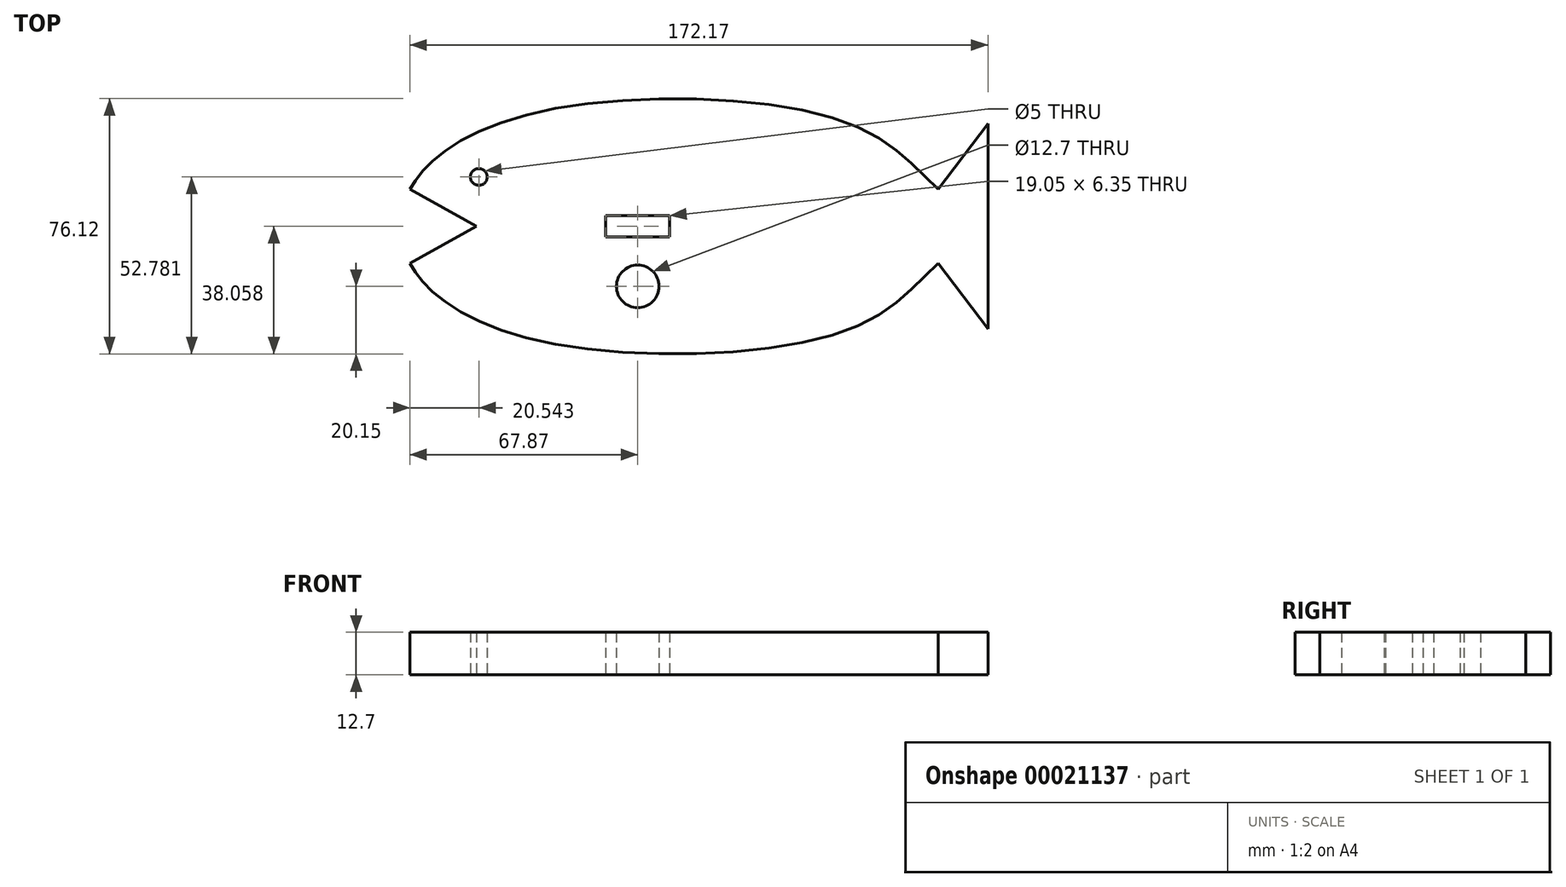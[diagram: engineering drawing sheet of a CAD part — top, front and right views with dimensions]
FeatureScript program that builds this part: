
annotation { "Feature Type Name" : "Feature", "Feature Type Description" : "" }
export const myFeature = defineFeature(function(context is Context, id is Id, definition is map)
    precondition{}
    {
        {
            var Q0;
            Q0=qCreatedBy(makeId("Top.planeOp"),FACE);
            var sketch = newSketch(context, id + "F0", { "sketchPlane" : qUnion([Q0])});
            skFitSpline(sketch, "E0", {"points": [v(89.47, 28.98) * mm, v(63.18, 48.55) * mm, v(-25.37, 52.9) * mm, v(-60.56, 37.87) * mm, v(-67.87, 28.98) * mm], "startDerivative": vector(-90.55, 84.73) * mm, "endDerivative": vector(-33.24, -55.1) * mm});
            skLineSegment(sketch, "E1", {"start": v(-67.87, 28.98) * mm, "end": v(-48.1, 17.9) * mm});
            skLineSegment(sketch, "E2", {"start": v(-48.1, 17.9) * mm, "end": v(104.3, 17.9) * mm, "construction": true});
            skLineSegment(sketch, "E3", {"start": v(89.47, 28.98) * mm, "end": v(104.3, 48.55) * mm});
            skLineSegment(sketch, "E4", {"start": v(104.3, 48.55) * mm, "end": v(104.3, 17.9) * mm});
            skLineSegment(sketch, "E5.MirrorCS", {"start": v(-67.87, 6.84) * mm, "end": v(-48.1, 17.9) * mm});
            skFitSpline(sketch, "E6.MirrorCS", {"points": [v(89.47, 6.84) * mm, v(63.18, -12.73) * mm, v(-25.37, -17.08) * mm, v(-60.56, -2.06) * mm, v(-67.87, 6.84) * mm], "startDerivative": vector(-90.55, -84.73) * mm, "endDerivative": vector(-33.24, 55.1) * mm});
            skLineSegment(sketch, "E7.MirrorCS", {"start": v(89.47, 6.84) * mm, "end": v(104.3, -12.73) * mm});
            skLineSegment(sketch, "E8.MirrorCS", {"start": v(104.3, -12.73) * mm, "end": v(104.3, 17.9) * mm});
            skCircle(sketch, "E9", {"center": v(-47.33, 32.63) * mm, "radius": 2.5 * mm});
            skLineSegment(sketch, "E10.rect.bottom", {"start": v(9.53, 21.08) * mm, "end": v(-9.53, 21.08) * mm});
            skLineSegment(sketch, "E10.rect.top", {"start": v(9.53, 14.73) * mm, "end": v(-9.53, 14.73) * mm});
            skLineSegment(sketch, "E10.rect.left", {"start": v(9.53, 21.08) * mm, "end": v(9.53, 14.73) * mm});
            skLineSegment(sketch, "E10.rect.right", {"start": v(-9.53, 21.08) * mm, "end": v(-9.53, 14.73) * mm});
            skPoint(sketch, "E10.rect.middle", {"position": v(0, 17.9) * mm});
            skCircle(sketch, "E11", {"center": v(0, 0) * mm, "radius": 6.35 * mm});
            skSolve(sketch);
        }
        {
            var Q0;
            Q0=makeQuery(id+"F0.imprint","IMPRINT",FACE,{"disambiguationData":[TD([[makeQuery(id+"F0.imprint","IMPRINT",EDGE,{"derivedFrom":sQuery(id+"F0.wireOp",EDGE,"E0")}),1.0]])]});
            extrude(context, id + "F1", {"entities" : qUnion([Q0]), "depth" : 12.7 * mm});
        }
    });
